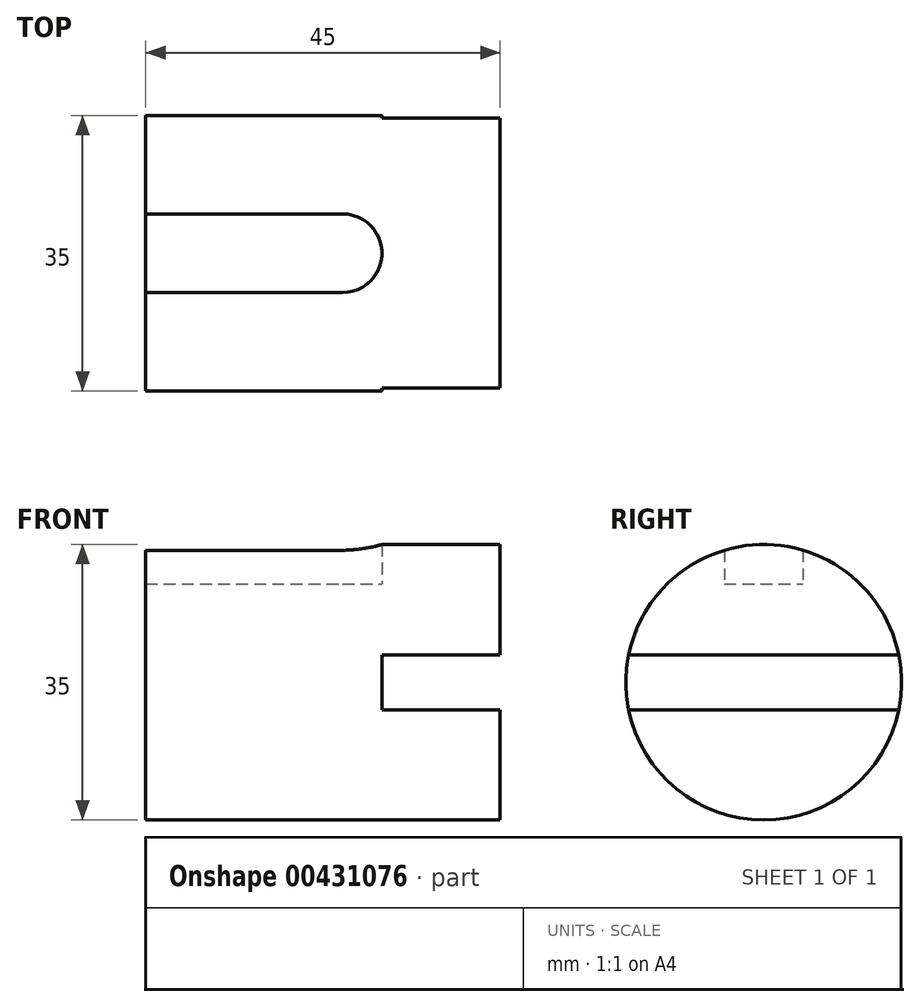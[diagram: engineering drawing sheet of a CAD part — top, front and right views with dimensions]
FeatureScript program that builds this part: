
annotation { "Feature Type Name" : "Feature", "Feature Type Description" : "" }
export const myFeature = defineFeature(function(context is Context, id is Id, definition is map)
    precondition{}
    {
        {
            var Q0;
            Q0=qCreatedBy(makeId("Right.planeOp"),FACE);
            var sketch = newSketch(context, id + "F0", { "sketchPlane" : qUnion([Q0])});
            skCircle(sketch, "E0", {"center": v(0, 0) * mm, "radius": 17.5 * mm});
            skSolve(sketch);
        }
        {
            var Q0;
            Q0=makeQuery(id+"F0.imprint","IMPRINT",FACE,{"disambiguationData":[TD([[makeQuery(id+"F0.imprint","IMPRINT",EDGE,{"derivedFrom":sQuery(id+"F0.wireOp",EDGE,"E0")}),1.0]])]});
            extrude(context, id + "F1", {"entities" : qUnion([Q0]), "depth" : 45 * mm});
        }
        {
            var Q0;
            Q0=makeQuery(id+"F1.opExtrude","CAP_FACE",FACE,{"disambiguationData":[OSD([sQuery(id+"F0.wireOp",EDGE,"E0")])],"isStart":false});
            var sketch = newSketch(context, id + "F2", { "sketchPlane" : qUnion([Q0])});
            skLineSegment(sketch, "E1", {"start": v(-17.15, 3.5) * mm, "end": v(17.15, 3.5) * mm});
            skLineSegment(sketch, "E2", {"start": v(-17.5, 0) * mm, "end": v(17.5, 0) * mm, "construction": true});
            skLineSegment(sketch, "E3", {"start": v(-17.15, -3.5) * mm, "end": v(17.15, -3.5) * mm});
            skArc(sketch, "E4.0", {"start": v(-17.15, 3.5) * mm, "mid": v(-17.5, 0) * mm, "end": v(-17.15, -3.5) * mm});
            skArc(sketch, "E5.trimOffspring", {"start": v(17.15, -3.5) * mm, "mid": v(17.5, 0) * mm, "end": v(17.15, 3.5) * mm});
            skSolve(sketch);
        }
        {
            var Q0;
            Q0=makeQuery(id+"F2.imprint","IMPRINT",FACE,{"disambiguationData":[TD([[makeQuery(id+"F2.imprint","IMPRINT",EDGE,{"derivedFrom":sQuery(id+"F2.wireOp",EDGE,"E1")}),-1.0]])]});
            extrude(context, id + "F3", {"entities" : qUnion([Q0]), "operationType" : NewBodyOperationType.REMOVE, "oppositeDirection" : true, "depth" : 15 * mm});
        }
        {
            var Q0;
            Q0=qCreatedBy(makeId("Top.planeOp"),FACE);
            cPlane(context, id + "F4", {"entities" : qUnion([Q0]), "cplaneType" : CPlaneType.OFFSET, "offset" : 12.5 * mm, "width" : 152.4 * mm, "height" : 152.4 * mm});
        }
        {
            var Q0;
            Q0=qCreatedBy(id+"F4.planeOp",FACE);
            var sketch = newSketch(context, id + "F5", { "sketchPlane" : qUnion([Q0])});
            skLineSegment(sketch, "E6", {"start": v(0, 0) * mm, "end": v(66.16, 0) * mm, "construction": true});
            skLineSegment(sketch, "E7", {"start": v(0, 5) * mm, "end": v(25, 5) * mm});
            skLineSegment(sketch, "E8", {"start": v(0, -5) * mm, "end": v(25, -5) * mm});
            skArc(sketch, "E9", {"start": v(25, 5) * mm, "mid": v(30, 0) * mm, "end": v(25, -5) * mm});
            skLineSegment(sketch, "E10", {"start": v(0, -5) * mm, "end": v(0, 5) * mm});
            skSolve(sketch);
        }
        {
            var Q0;
            Q0 = qSketchRegion(id + "F5", true);
            extrude(context, id + "F6", {"entities" : qUnion([Q0]), "operationType" : NewBodyOperationType.REMOVE, "depth" : 10 * mm});
        }
    });
